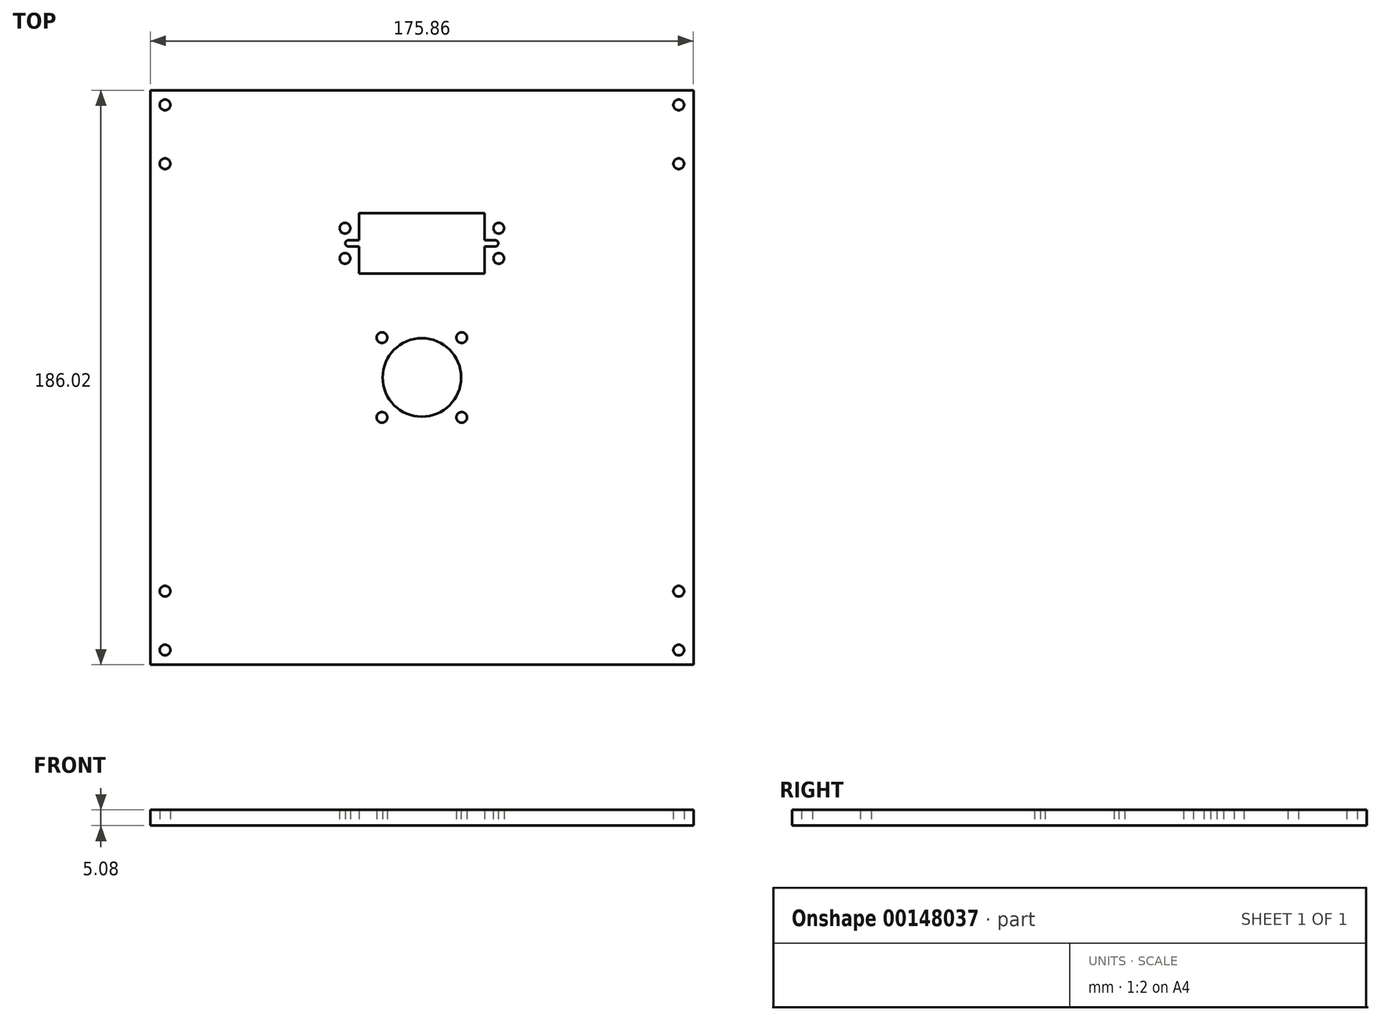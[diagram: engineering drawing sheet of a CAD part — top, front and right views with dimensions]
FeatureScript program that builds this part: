
annotation { "Feature Type Name" : "Feature", "Feature Type Description" : "" }
export const myFeature = defineFeature(function(context is Context, id is Id, definition is map)
    precondition{}
    {
        {
            var Q0;
            Q0=qCreatedBy(makeId("Top.planeOp"),FACE);
            var sketch = newSketch(context, id + "F0", { "sketchPlane" : qUnion([Q0])});
            skLineSegment(sketch, "E0.bottom", {"start": v(-12.9, 12.9) * mm, "end": v(12.9, 12.9) * mm, "construction": true});
            skLineSegment(sketch, "E0.top", {"start": v(-12.9, -12.9) * mm, "end": v(12.9, -12.9) * mm, "construction": true});
            skLineSegment(sketch, "E0.left", {"start": v(-12.9, 12.9) * mm, "end": v(-12.9, -12.9) * mm, "construction": true});
            skLineSegment(sketch, "E0.right", {"start": v(12.9, 12.9) * mm, "end": v(12.9, -12.9) * mm, "construction": true});
            skPoint(sketch, "E0.middle", {"position": v(0, 0) * mm});
            skCircle(sketch, "E1", {"center": v(0, 0) * mm, "radius": 14.29 * mm, "construction": true});
            skCircle(sketch, "E2", {"center": v(-12.9, 12.9) * mm, "radius": 3.97 * mm, "construction": true});
            skCircle(sketch, "E3", {"center": v(-12.9, 12.9) * mm, "radius": 1.73 * mm});
            skCircle(sketch, "E4", {"center": v(12.9, 12.9) * mm, "radius": 1.73 * mm});
            skCircle(sketch, "E5", {"center": v(12.9, -12.9) * mm, "radius": 1.73 * mm});
            skCircle(sketch, "E6", {"center": v(-12.9, -12.9) * mm, "radius": 1.73 * mm});
            skLineSegment(sketch, "E7", {"start": v(0, 0) * mm, "end": v(0, 0) * mm});
            skLineSegment(sketch, "E8.bottom", {"start": v(-87.93, 93.01) * mm, "end": v(87.93, 93.01) * mm});
            skLineSegment(sketch, "E8.top", {"start": v(-87.93, -93.01) * mm, "end": v(87.93, -93.01) * mm});
            skLineSegment(sketch, "E8.left", {"start": v(-87.93, 93.01) * mm, "end": v(-87.93, -93.01) * mm});
            skLineSegment(sketch, "E8.right", {"start": v(87.93, 93.01) * mm, "end": v(87.93, -93.01) * mm});
            skLineSegment(sketch, "E9", {"start": v(-87.93, 88.25) * mm, "end": v(-83.17, 88.25) * mm, "construction": true});
            skLineSegment(sketch, "E10", {"start": v(-83.17, 88.25) * mm, "end": v(-83.17, 93.01) * mm, "construction": true});
            skLineSegment(sketch, "E11", {"start": v(-83.17, -93.01) * mm, "end": v(-83.17, -88.25) * mm, "construction": true});
            skLineSegment(sketch, "E12", {"start": v(-83.17, -88.25) * mm, "end": v(-83.17, -69.2) * mm, "construction": true});
            skLineSegment(sketch, "E13", {"start": v(83.17, 93.01) * mm, "end": v(83.17, 88.25) * mm, "construction": true});
            skLineSegment(sketch, "E14", {"start": v(83.17, 88.25) * mm, "end": v(87.93, 88.25) * mm, "construction": true});
            skLineSegment(sketch, "E15", {"start": v(83.17, 88.25) * mm, "end": v(83.17, 69.2) * mm, "construction": true});
            skLineSegment(sketch, "E16", {"start": v(-83.17, 88.25) * mm, "end": v(-83.17, 69.2) * mm, "construction": true});
            skLineSegment(sketch, "E17", {"start": v(83.17, -93.01) * mm, "end": v(83.17, -88.25) * mm, "construction": true});
            skLineSegment(sketch, "E18", {"start": v(83.17, -88.25) * mm, "end": v(83.17, -69.2) * mm, "construction": true});
            skCircle(sketch, "E19", {"center": v(-83.17, 88.25) * mm, "radius": 1.73 * mm});
            skCircle(sketch, "E20", {"center": v(-83.17, 69.2) * mm, "radius": 1.73 * mm});
            skCircle(sketch, "E21", {"center": v(-83.17, -69.2) * mm, "radius": 1.73 * mm});
            skCircle(sketch, "E22", {"center": v(-83.17, -88.25) * mm, "radius": 1.73 * mm});
            skCircle(sketch, "E23", {"center": v(83.17, -88.25) * mm, "radius": 1.73 * mm});
            skCircle(sketch, "E24", {"center": v(83.17, -69.2) * mm, "radius": 1.73 * mm});
            skCircle(sketch, "E25", {"center": v(83.17, 69.2) * mm, "radius": 1.73 * mm});
            skCircle(sketch, "E26", {"center": v(83.17, 88.25) * mm, "radius": 1.73 * mm});
            skLineSegment(sketch, "E27", {"start": v(0, 0) * mm, "end": v(0, 33.66) * mm, "construction": true});
            skLineSegment(sketch, "E28", {"start": v(0, 33.66) * mm, "end": v(0, 53.22) * mm, "construction": true});
            skLineSegment(sketch, "E29", {"start": v(-20.32, 53.22) * mm, "end": v(20.32, 53.22) * mm});
            skLineSegment(sketch, "E30", {"start": v(-20.32, 33.66) * mm, "end": v(20.32, 33.66) * mm});
            skLineSegment(sketch, "E31", {"start": v(-20.32, 53.22) * mm, "end": v(-20.32, 44.45) * mm});
            skLineSegment(sketch, "E32", {"start": v(-20.32, 33.66) * mm, "end": v(-20.32, 42.42) * mm});
            skLineSegment(sketch, "E33", {"start": v(20.32, 33.66) * mm, "end": v(20.32, 42.42) * mm});
            skLineSegment(sketch, "E34", {"start": v(20.32, 53.22) * mm, "end": v(20.32, 44.45) * mm});
            skLineSegment(sketch, "E35.bottom", {"start": v(20.32, 44.45) * mm, "end": v(23.75, 44.45) * mm});
            skLineSegment(sketch, "E35.top", {"start": v(20.32, 42.42) * mm, "end": v(23.75, 42.42) * mm});
            skLineSegment(sketch, "E35.left", {"start": v(20.32, 44.45) * mm, "end": v(20.32, 42.42) * mm, "construction": true});
            skLineSegment(sketch, "E35.right", {"start": v(23.75, 44.45) * mm, "end": v(23.75, 42.42) * mm, "construction": true});
            skLineSegment(sketch, "E36.bottom", {"start": v(-20.32, 44.45) * mm, "end": v(-23.75, 44.45) * mm});
            skLineSegment(sketch, "E36.top", {"start": v(-20.32, 42.42) * mm, "end": v(-23.75, 42.42) * mm});
            skLineSegment(sketch, "E36.left", {"start": v(-20.32, 44.45) * mm, "end": v(-20.32, 42.42) * mm, "construction": true});
            skLineSegment(sketch, "E36.right", {"start": v(-23.75, 44.45) * mm, "end": v(-23.75, 42.42) * mm, "construction": true});
            skLineSegment(sketch, "E37.bottom", {"start": v(-24.9, 48.33) * mm, "end": v(24.9, 48.33) * mm, "construction": true});
            skLineSegment(sketch, "E37.top", {"start": v(-24.9, 38.55) * mm, "end": v(24.9, 38.55) * mm, "construction": true});
            skLineSegment(sketch, "E37.left", {"start": v(-24.9, 48.33) * mm, "end": v(-24.9, 38.55) * mm, "construction": true});
            skLineSegment(sketch, "E37.right", {"start": v(24.9, 48.33) * mm, "end": v(24.9, 38.55) * mm, "construction": true});
            skPoint(sketch, "E37.middle", {"position": v(0, 43.44) * mm});
            skArc(sketch, "E38", {"start": v(-23.75, 44.45) * mm, "mid": v(-24.77, 43.44) * mm, "end": v(-23.75, 42.42) * mm});
            skArc(sketch, "E39", {"start": v(23.75, 42.42) * mm, "mid": v(24.77, 43.44) * mm, "end": v(23.75, 44.45) * mm});
            skCircle(sketch, "E40", {"center": v(-24.9, 48.33) * mm, "radius": 1.73 * mm});
            skCircle(sketch, "E41", {"center": v(-24.9, 38.55) * mm, "radius": 1.73 * mm});
            skCircle(sketch, "E42", {"center": v(24.9, 38.55) * mm, "radius": 1.73 * mm});
            skCircle(sketch, "E43", {"center": v(24.9, 48.33) * mm, "radius": 1.73 * mm});
            skCircle(sketch, "E44", {"center": v(0, 0) * mm, "radius": 12.7 * mm});
            skLineSegment(sketch, "E45", {"start": v(20.32, 43.44) * mm, "end": v(10.9, 43.44) * mm, "construction": true});
            skLineSegment(sketch, "E46", {"start": v(10.9, 43.44) * mm, "end": v(0, 0) * mm, "construction": true});
            skSolve(sketch);
        }
        {
            var Q0;
            Q0=qSketchRegion(id+"F0",true);
            extrude(context, id + "F1", {"entities" : qUnion([Q0]), "depth" : 5.08 * mm});
        }
    });
